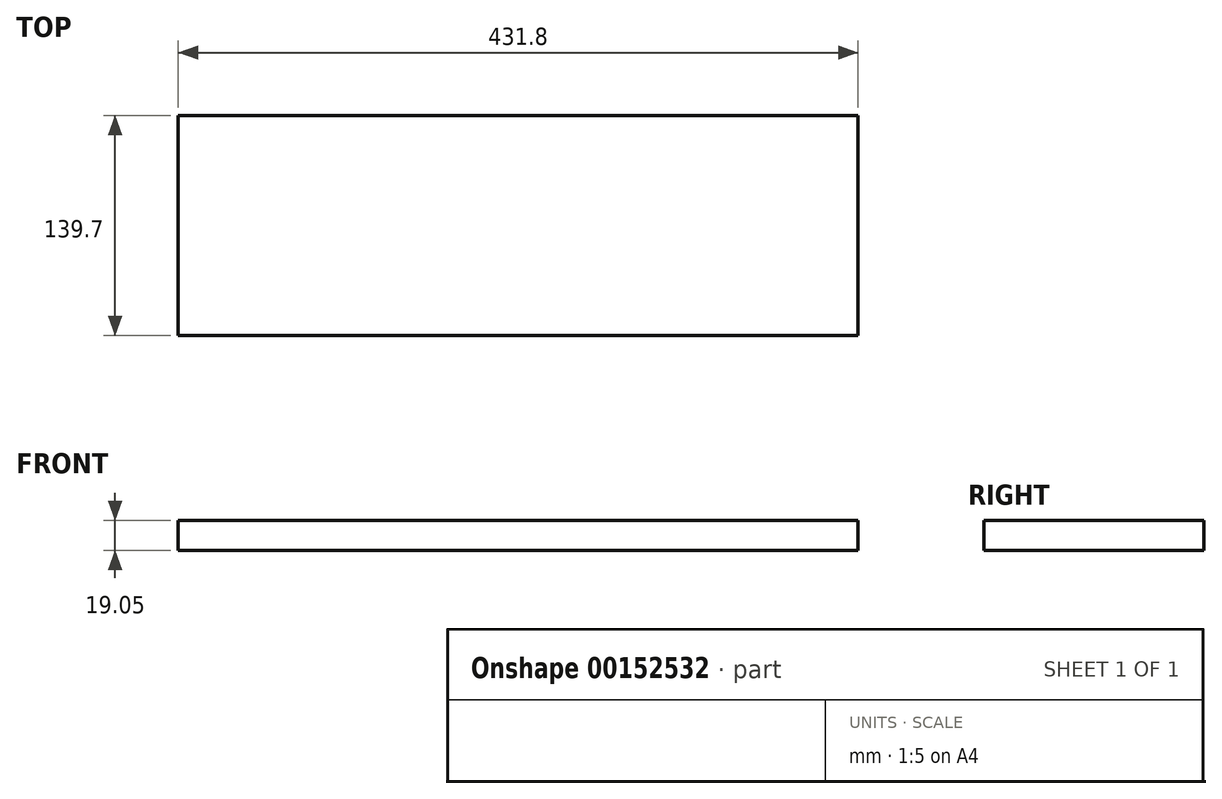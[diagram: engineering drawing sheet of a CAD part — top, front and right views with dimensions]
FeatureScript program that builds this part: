
annotation { "Feature Type Name" : "Feature", "Feature Type Description" : "" }
export const myFeature = defineFeature(function(context is Context, id is Id, definition is map)
    precondition{}
    {
        {
            var Q0;
            Q0=qCreatedBy(makeId("Top.planeOp"),FACE);
            var sketch = newSketch(context, id + "F0", { "sketchPlane" : qUnion([Q0])});
            skLineSegment(sketch, "E0.bottom", {"start": v(-215.9, 69.85) * mm, "end": v(215.9, 69.85) * mm});
            skLineSegment(sketch, "E0.top", {"start": v(-215.9, -69.85) * mm, "end": v(215.9, -69.85) * mm});
            skLineSegment(sketch, "E0.left", {"start": v(-215.9, 69.85) * mm, "end": v(-215.9, -69.85) * mm});
            skLineSegment(sketch, "E0.right", {"start": v(215.9, 69.85) * mm, "end": v(215.9, -69.85) * mm});
            skLineSegment(sketch, "E1", {"start": v(0, 69.85) * mm, "end": v(0, -69.85) * mm, "construction": true});
            skSolve(sketch);
        }
        {
            var Q0;
            Q0 = qSketchRegion(id + "F0", true);
            extrude(context, id + "F1", {"entities" : qUnion([Q0]), "depth" : 19.05 * mm});
        }
    });
